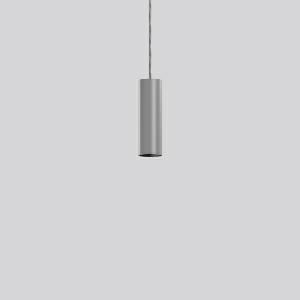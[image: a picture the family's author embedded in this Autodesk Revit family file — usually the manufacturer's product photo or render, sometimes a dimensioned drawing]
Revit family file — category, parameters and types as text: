
# Revit family: deecos_p_micro_911489_004_2_76_2caa
name_source: partatom
category: Lighting Fixtures
units: mm (PartAtom-declared; Revit-internal decimal feet)

## family parameters
Cut with Voids When Loaded = No
Host = Face
Light Source = No
Part Type = Normal
Room Calculation Point = No
Round Connector Dimension = Use Diameter
Shared = No

## types (1)
- DEECOS P micro (1 x LED Modul 940, 1850 lm, 4000)
    Apparent Load = 16 VA
    CIE Flux Codes = 98 100 100 100 100
    Color Rendering = 92
    Color Temperature = 4000
    Default Elevation = 1800 mm
    Description = Series: DEECOS P micro
Cylindrical pendant luminaire. Housing: die-cast aluminium, powder-coated. Canopy made of powder-coated sheet steel with magnetic attachment. Optical assembly with reflector made of MIRO-Silver with 98% total light reflection for outstanding efficiency - can be changed without tools. Black plastic ring and recessed LED to prevent glare from the side. Best colour rendering index Ra>90. Transparent suspension cable 3 m, can be shortened. High quality converter without flickering and stroboscopic effect. 
Colour: silver
Diameter: 60 mm
Height: 190 mm
Suspension length: 3000 mm
Lamp: LED
Socket: without socket
Colour temperature: 4000K
Colour rendering index (CRI): 92
System power: 16 W
Rated luminous flux: 1850 lm
Luminous efficiency: 116 lm/W
Control gear: Converter, dimmable, DALI
Protection class: I
Type of protection: IP 20
    Height = 190 mm  [stored 0.62336 ft]
    Lamp = 1 x LED Modul 940
    Lamp Light Flux = 1850 lm
    Lamp count = 1
    Length = 60 mm  [stored 0.19685 ft]
    Lifetime = 50000 h
    Luminous efficacy = 116 lm/W
    Manufacturer = RZB
    ModVariant = No
    Model = 911489.004.2.76
    Mounting Place = Ceiling
    Mounting Type = Pendant
    Number of Poles = 1
    OnlyDefault = Yes
    Power Factor = 1
    Product Name = DEECOS P micro
    Product group = Pendant luminaires
    ProductGroupID = 902
    Protection Class = Protection class I
    Protection Degree = Degree of protection
    RLX_Detail_Level = 1
    RLX_Emergency_Light_Flux = 0 lm
    RLX_Emergency_Type = 0
    RLX_Emergency_Type_DB = No
    RlxData = <blob elided: 31221 chars, md5=026201b5>
    Socket = socket
    Standby Power = 0 W
    System Light Flux = 1850 lm
    System Power = 16 W
    Type Comments = Product without accessories
    Type Image = 911489.004.jpg
    URL = http://relux.com
    VarID = ---
    Voltage = 0 V
    Weight = 0.00 kg
    Width = 0 mm  [stored 0 ft]

note: [stored X ft] marks values corroborated as IEEE doubles in the binary element streams (Revit-internal decimal feet)

## geometry (parser evidence)
native form markers: Blend x4, Sweep x9
no freeform markers — native parametric forms only
